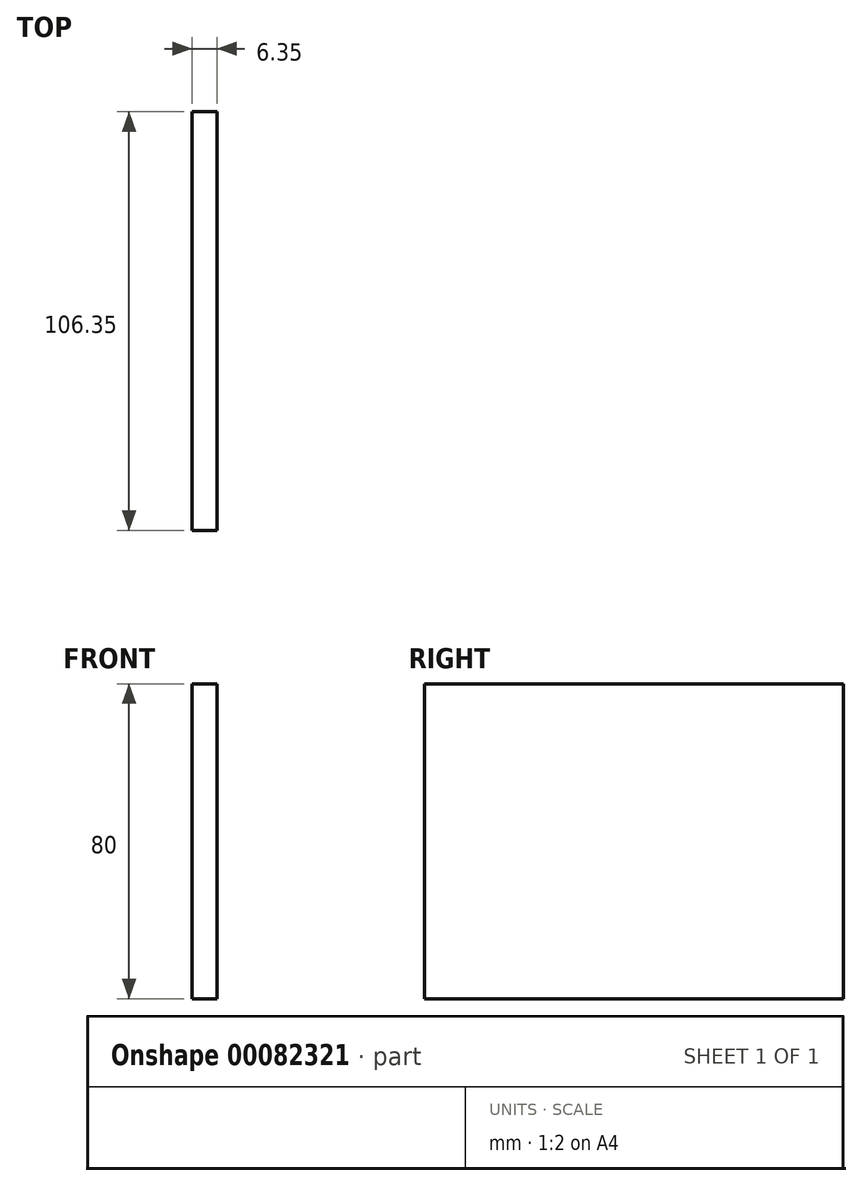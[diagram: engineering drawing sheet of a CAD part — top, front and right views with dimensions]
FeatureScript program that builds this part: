
annotation { "Feature Type Name" : "Feature", "Feature Type Description" : "" }
export const myFeature = defineFeature(function(context is Context, id is Id, definition is map)
    precondition{}
    {
        {
            var Q0;
            Q0=qCreatedBy(makeId("Right.planeOp"),FACE);
            var sketch = newSketch(context, id + "F0", { "sketchPlane" : qUnion([Q0])});
            skLineSegment(sketch, "E0.bottom", {"start": v(50, -37.5) * mm, "end": v(-50, -37.5) * mm});
            skLineSegment(sketch, "E0.top", {"start": v(50, 37.5) * mm, "end": v(-50, 37.5) * mm});
            skLineSegment(sketch, "E0.left", {"start": v(50, -37.5) * mm, "end": v(50, 37.5) * mm});
            skLineSegment(sketch, "E0.right", {"start": v(-50, -37.5) * mm, "end": v(-50, 37.5) * mm});
            skPoint(sketch, "E0.middle", {"position": v(0, 0) * mm});
            skCircle(sketch, "E1", {"center": v(-39.38, -27.5) * mm, "radius": 2.39 * mm});
            skLineSegment(sketch, "E2.bottom", {"start": v(-50, 37.5) * mm, "end": v(-56.35, 37.5) * mm});
            skLineSegment(sketch, "E2.top", {"start": v(-50, -37.5) * mm, "end": v(-56.35, -37.5) * mm});
            skLineSegment(sketch, "E2.left", {"start": v(-50, 37.5) * mm, "end": v(-50, -37.5) * mm});
            skLineSegment(sketch, "E2.right", {"start": v(-56.35, 37.5) * mm, "end": v(-56.35, -37.5) * mm});
            skLineSegment(sketch, "E3.bottom", {"start": v(-56.35, 37.5) * mm, "end": v(50, 37.5) * mm});
            skLineSegment(sketch, "E3.top", {"start": v(-56.35, 42.5) * mm, "end": v(50, 42.5) * mm});
            skLineSegment(sketch, "E3.left", {"start": v(-56.35, 37.5) * mm, "end": v(-56.35, 42.5) * mm});
            skLineSegment(sketch, "E3.right", {"start": v(50, 37.5) * mm, "end": v(50, 42.5) * mm});
            skSolve(sketch);
        }
        {
            var Q0;
            Q0=qSketchRegion(id+"F0",true);
            var Q1;
            Q1=makeQuery(id+"F0.imprint","IMPRINT",FACE,{"disambiguationData":[TD([[makeQuery(id+"F0.imprint","IMPRINT",EDGE,{"derivedFrom":sQuery(id+"F0.wireOp",EDGE,"E1")}),1.0]])]});
            extrude(context, id + "F1", {"entities" : qUnion([Q0, Q1]), "depth" : 6.35 * mm});
        }
    });
